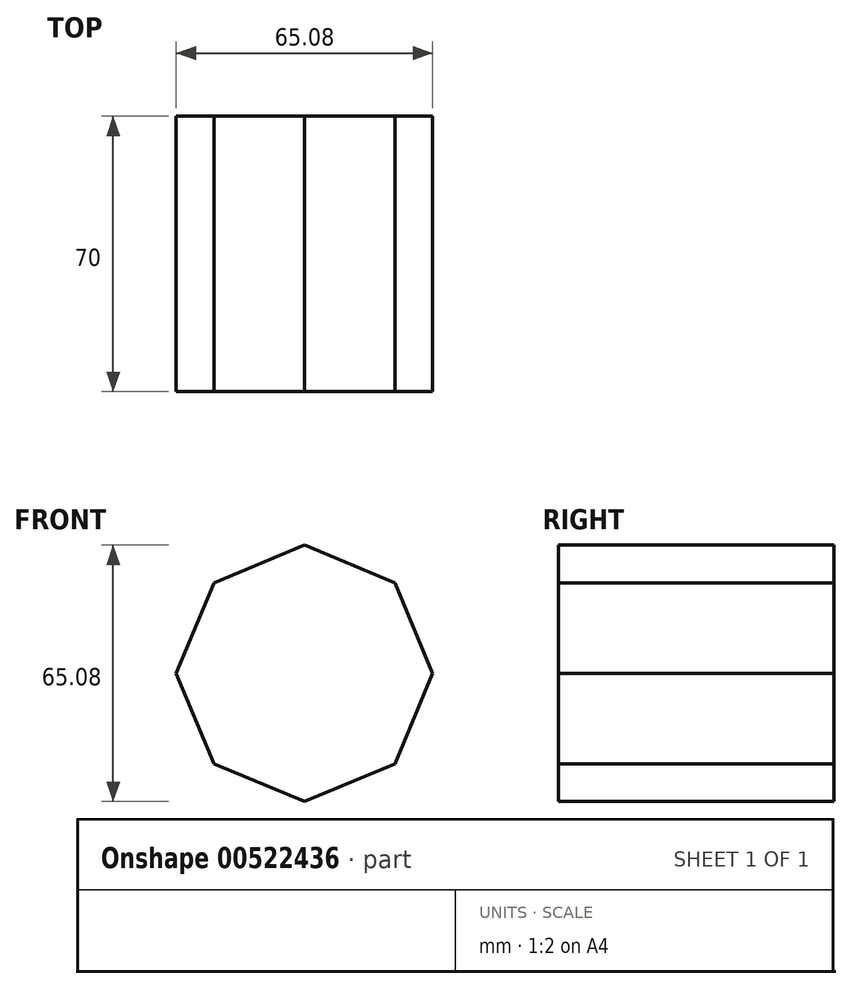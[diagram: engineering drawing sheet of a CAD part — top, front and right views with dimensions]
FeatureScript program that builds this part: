
annotation { "Feature Type Name" : "Feature", "Feature Type Description" : "" }
export const myFeature = defineFeature(function(context is Context, id is Id, definition is map)
    precondition{}
    {
        {
            var Q0;
            Q0=qCreatedBy(makeId("Front.planeOp"),FACE);
            var sketch = newSketch(context, id + "F0", { "sketchPlane" : qUnion([Q0])});
            skCircle(sketch, "E0.cCircle", {"center": v(0, 0) * mm, "radius": 32.54 * mm, "construction": true});
            skLineSegment(sketch, "E0.0", {"start": v(-32.54, 0) * mm, "end": v(-23, 23) * mm});
            skLineSegment(sketch, "E0.1", {"start": v(-23, 23) * mm, "end": v(0, 32.54) * mm});
            skLineSegment(sketch, "E0.2", {"start": v(0, 32.54) * mm, "end": v(23, 23) * mm});
            skLineSegment(sketch, "E0.3", {"start": v(23, 23) * mm, "end": v(32.54, 0) * mm});
            skLineSegment(sketch, "E0.4", {"start": v(32.54, 0) * mm, "end": v(23, -23) * mm});
            skLineSegment(sketch, "E0.5", {"start": v(23, -23) * mm, "end": v(0, -32.54) * mm});
            skLineSegment(sketch, "E0.6", {"start": v(0, -32.54) * mm, "end": v(-23, -23) * mm});
            skLineSegment(sketch, "E0.7", {"start": v(-23, -23) * mm, "end": v(-32.54, 0) * mm});
            skSolve(sketch);
        }
        {
            var Q0;
            Q0=makeQuery(id+"F0.imprint","IMPRINT",FACE,{"disambiguationData":[TD([[makeQuery(id+"F0.imprint","IMPRINT",EDGE,{"derivedFrom":sQuery(id+"F0.wireOp",EDGE,"E0.0")}),-1.0]])]});
            extrude(context, id + "F1", {"entities" : qUnion([Q0]), "depth" : 70 * mm, "offsetDistance" : 25 * mm});
        }
    });
